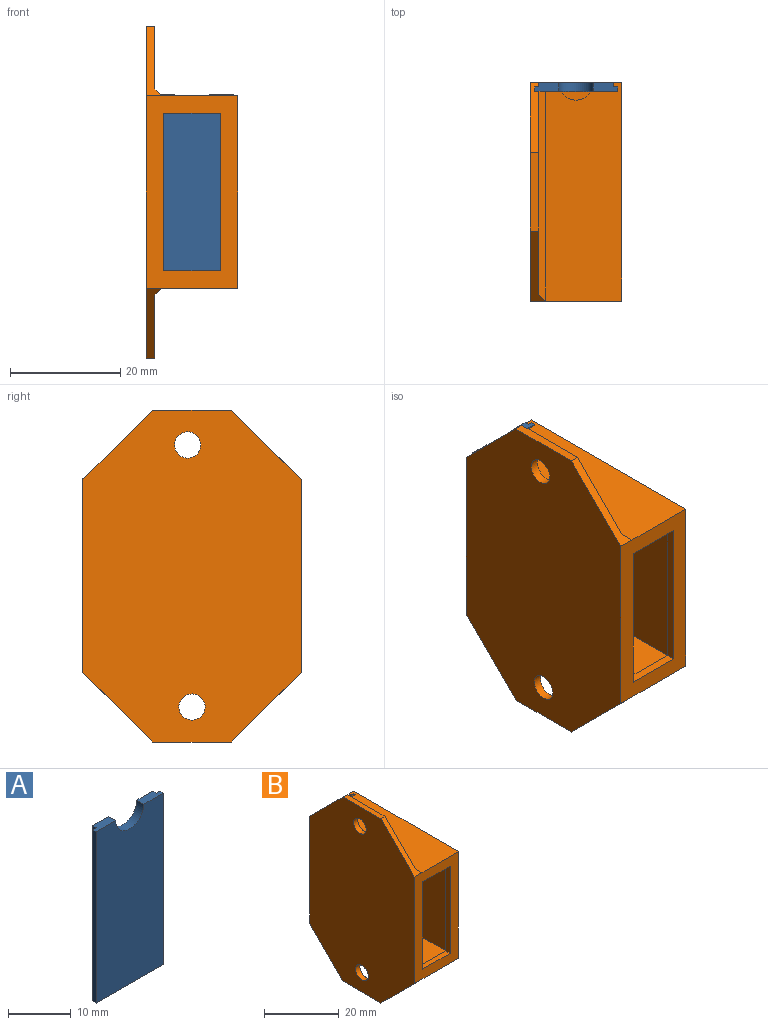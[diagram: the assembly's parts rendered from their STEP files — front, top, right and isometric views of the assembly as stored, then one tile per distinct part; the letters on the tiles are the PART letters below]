
ASSEMBLY  parts=2 mates=2
PART A: 12 faces, bbox 15.1x1.6x33.3 mm
  f0: plane 4.37x1.59mm, normal (0,0,1), area 6.3mm2, adj f1,f2,f6,f7,f8,f11
  f1: plane 33.34x0.79mm, normal (-1,0,0), area 26.5mm2, adj f0,f2,f8,f10
  f2: plane 33.34x15.08mm, normal (0,-1,0), area 486.9mm2, adj f0,f1,f3,f9,f10,f11
  f3: plane 33.34x0.79mm, normal (1,0,0), area 26.5mm2, adj f2,f4,f9,f10
  f4: plane 33.34x0.79mm, normal (0,1,0), area 26.5mm2, adj f3,f5,f9,f10
  f5: plane 33.34x0.79mm, normal (1,0,0), area 26.5mm2, adj f4,f6,f9,f10
  f6: plane 33.34x13.49mm, normal (0,1,0), area 434mm2, adj f0,f5,f7,f9,f10,f11
  f7: plane 33.34x0.79mm, normal (-1,0,0), area 26.5mm2, adj f0,f6,f8,f10
  f8: plane 33.34x0.79mm, normal (0,1,0), area 26.5mm2, adj f0,f1,f7,f10
  f9: plane 4.37x1.59mm, normal (0,0,1), area 6.3mm2, adj f2,f3,f4,f5,f6,f11
  f10: plane 15.08x1.59mm, normal (0,0,-1), area 22.7mm2, adj f1,f2,f3,f4,f5,f6,f7,f8
  f11: cylinder r=3.17mm len=6.35mm, axis (0,-1,0), area 15.8mm2, adj f0,f2,f6,f9
PART B: 36 faces, bbox 16.7x39.7x60.3 mm
  f0: plane 33.34x0.79mm, normal (-1,0,0), area 26.5mm2, adj f1,f3,f16,f33
  f1: plane 34.93x16.67mm, normal (0,1,0), area 132.3mm2, adj f0,f2,f3,f4,f5,f10,f16,f19
  f2: plane 34.13x0.79mm, normal (1,0,0), area 26.8mm2, adj f1,f16,f19,f30
  f3: plane 39.69x13.81mm, normal (0,0,1), area 521.9mm2, adj f0,f1,f10,f11,f27,f29,f31,f32
  f4: plane 60.33x39.69mm, normal (-1,0,0), area 2035.9mm2, adj f1,f11,f17,f18,f19,f20,f22,f23
  f5: plane 39.69x13.81mm, normal (0,0,-1), area 548.1mm2, adj f1,f10,f11,f35
  f6: plane 28.58x1.59mm, normal (1,0,0), area 45.4mm2, adj f7,f9,f11,f12
  f7: plane 10.32x1.59mm, normal (0,0,-1), area 16.4mm2, adj f6,f8,f11,f12
  f8: plane 28.58x1.59mm, normal (-1,0,0), area 45.4mm2, adj f7,f9,f11,f12
  f9: plane 10.32x1.59mm, normal (0,0,1), area 16.4mm2, adj f6,f8,f11,f12
  f10: plane 39.69x34.93mm, normal (1,0,0), area 1386.1mm2, adj f1,f3,f5,f11
  f11: plane 34.93x16.67mm, normal (0,-1,0), area 287.3mm2, adj f3,f4,f5,f6,f7,f8,f9,f10
  f12: plane 31.75x13.49mm, normal (0,1,0), area 133.6mm2, adj f6,f7,f8,f9,f13,f14,f15,f16
  f13: plane 36.51x31.75mm, normal (-1,0,0), area 1159.3mm2, adj f12,f14,f16,f31
  f14: plane 36.51x13.49mm, normal (0,0,-1), area 486.5mm2, adj f12,f13,f15,f27,f29,f31
  f15: plane 36.51x31.75mm, normal (1,0,0), area 1159.3mm2, adj f12,f14,f16,f29
  f16: plane 38.1x15.08mm, normal (0,0,1), area 515.4mm2, adj f0,f1,f2,f12,f13,f15,f28,f29
  f17: plane 12.7x12.7mm, normal (0,-0.71,0.71), area 29.7mm2, adj f4,f11,f18,f21,f34
  f18: plane 14.29x1.59mm, normal (0,0,1), area 22.7mm2, adj f4,f17,f19,f21
  f19: plane 12.7x12.7mm, normal (0,0.71,0.71), area 27.6mm2, adj f1,f2,f4,f18,f21,f28,f29,f30
  f20: cylinder r=2.38mm len=4.76mm, axis (-1,0,0), area 23.8mm2, adj f4,f21
  f21: plane 36.83x11.43mm, normal (1,0,0), area 276.1mm2, adj f17,f18,f19,f20,f29,f34
  f22: plane 12.7x12.7mm, normal (0,0.71,-0.71), area 29.7mm2, adj f1,f4,f23,f26,f35
  f23: plane 14.29x1.59mm, normal (0,0,-1), area 22.7mm2, adj f4,f22,f25,f26
  f24: cylinder r=2.38mm len=4.76mm, axis (-1,0,0), area 23.8mm2, adj f4,f26
  f25: plane 12.7x12.7mm, normal (0,-0.71,-0.71), area 29.7mm2, adj f4,f11,f23,f26,f35
  f26: plane 37.15x11.43mm, normal (1,0,0), area 276.1mm2, adj f22,f23,f24,f25,f35
  f27: cylinder r=3.17mm len=5.5mm, axis (0,0,1), area 10.6mm2, adj f3,f14,f29,f31
  f28: plane 34.93x0.79mm, normal (1,0,0), area 27.4mm2, adj f16,f19,f29,f30
  f29: plane 34.93x4.79mm, normal (0,1,0), area 34.9mm2, adj f3,f14,f15,f16,f19,f21,f27,f28
  f30: plane 34.13x0.79mm, normal (0,-1,0), area 27.1mm2, adj f2,f16,f19,f28
  f31: plane 33.34x4.79mm, normal (0,1,0), area 32.8mm2, adj f3,f13,f14,f16,f27,f32
  f32: plane 33.34x0.79mm, normal (-1,0,0), area 26.5mm2, adj f3,f16,f31,f33
  f33: plane 33.34x0.79mm, normal (0,-1,0), area 26.5mm2, adj f0,f3,f16,f32
  f34: plane 38.1x1.27mm, normal (0.71,0,0.71), area 67.3mm2, adj f3,f17,f21,f29
  f35: plane 39.69x1.27mm, normal (0.71,0,-0.71), area 69mm2, adj f5,f22,f25,f26
PLACE A t=(0.56,19.16,-23.14)mm
PLACE B t=(8.1,-17.35,-7.47)mm
MATE fastened B.f2 <-> A.f7  axis (1,0,0) through (1.35,20.35,-6.47)mm
MATE fastened B.f1 <-> B.f2  axis (0,1,0) through (8.1,20.75,-10.17)mm
